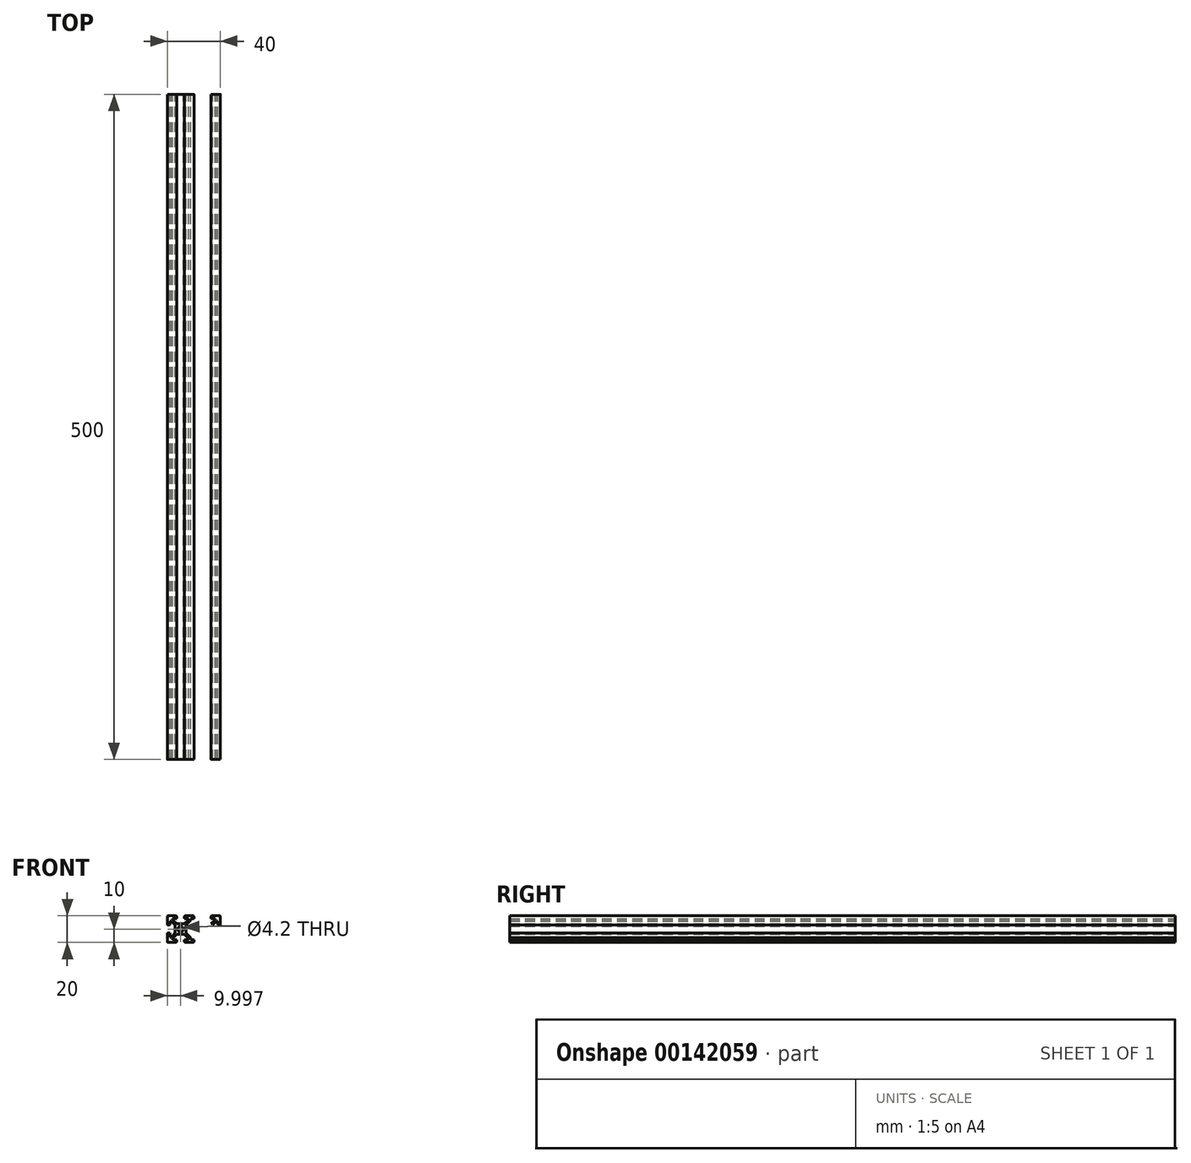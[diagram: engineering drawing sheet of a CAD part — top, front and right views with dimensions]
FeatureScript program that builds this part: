
annotation { "Feature Type Name" : "Feature", "Feature Type Description" : "" }
export const myFeature = defineFeature(function(context is Context, id is Id, definition is map)
    precondition{}
    {
        {
            var Q0;
            Q0=qCreatedBy(makeId("Front.planeOp"),FACE);
            var sketch = newSketch(context, id + "F0", { "sketchPlane" : qUnion([Q0])});
            skLineSegment(sketch, "E0.bottom", {"start": v(-257.68, 19.3) * mm, "end": v(-217.68, 19.3) * mm});
            skLineSegment(sketch, "E0.top", {"start": v(-257.68, -0.7) * mm, "end": v(-217.68, -0.7) * mm});
            skLineSegment(sketch, "E0.left", {"start": v(-257.68, 19.3) * mm, "end": v(-257.68, -0.7) * mm});
            skLineSegment(sketch, "E0.right", {"start": v(-217.68, 19.3) * mm, "end": v(-217.68, -0.7) * mm});
            skLineSegment(sketch, "E1.bottom", {"start": v(-251.68, 13.3) * mm, "end": v(-243.68, 13.3) * mm});
            skLineSegment(sketch, "E1.top", {"start": v(-251.68, 5.3) * mm, "end": v(-243.68, 5.3) * mm});
            skLineSegment(sketch, "E1.left", {"start": v(-251.68, 13.3) * mm, "end": v(-251.68, 5.3) * mm});
            skLineSegment(sketch, "E1.right", {"start": v(-243.68, 13.3) * mm, "end": v(-243.68, 5.3) * mm});
            skLineSegment(sketch, "E2.bottom", {"start": v(-231.68, 13.3) * mm, "end": v(-223.68, 13.3) * mm});
            skLineSegment(sketch, "E2.top", {"start": v(-231.68, 5.3) * mm, "end": v(-223.68, 5.3) * mm});
            skLineSegment(sketch, "E2.left", {"start": v(-231.68, 13.3) * mm, "end": v(-231.68, 5.3) * mm});
            skLineSegment(sketch, "E2.right", {"start": v(-223.68, 13.3) * mm, "end": v(-223.68, 5.3) * mm});
            skCircle(sketch, "E3", {"center": v(-247.68, 9.3) * mm, "radius": 4 * mm});
            skPoint(sketch, "E3.first.point", {"position": v(-251.68, 9.3) * mm});
            skPoint(sketch, "E3.second.point", {"position": v(-247.68, 5.3) * mm});
            skPoint(sketch, "E3.third.point", {"position": v(-243.68, 9.3) * mm});
            skCircle(sketch, "E4", {"center": v(-227.68, 9.3) * mm, "radius": 4 * mm});
            skPoint(sketch, "E4.first.point", {"position": v(-227.68, 5.3) * mm});
            skPoint(sketch, "E4.second.point", {"position": v(-231.68, 9.3) * mm});
            skPoint(sketch, "E4.third.point", {"position": v(-227.68, 13.3) * mm});
            skCircle(sketch, "E5", {"center": v(-247.68, 9.3) * mm, "radius": 2.1 * mm});
            skCircle(sketch, "E6", {"center": v(-227.68, 9.3) * mm, "radius": 2.1 * mm});
            skLineSegment(sketch, "E7.bottom", {"start": v(-250.68, -0.7) * mm, "end": v(-244.68, -0.7) * mm});
            skLineSegment(sketch, "E7.top", {"start": v(-250.68, 1.3) * mm, "end": v(-244.68, 1.3) * mm});
            skLineSegment(sketch, "E7.left", {"start": v(-250.68, -0.7) * mm, "end": v(-250.68, 1.3) * mm});
            skLineSegment(sketch, "E7.right", {"start": v(-244.68, -0.7) * mm, "end": v(-244.68, 1.3) * mm});
            skLineSegment(sketch, "E8.bottom", {"start": v(-230.68, -0.7) * mm, "end": v(-224.68, -0.7) * mm});
            skLineSegment(sketch, "E8.top", {"start": v(-230.68, 1.3) * mm, "end": v(-224.68, 1.3) * mm});
            skLineSegment(sketch, "E8.left", {"start": v(-230.68, -0.7) * mm, "end": v(-230.68, 1.3) * mm});
            skLineSegment(sketch, "E8.right", {"start": v(-224.68, -0.7) * mm, "end": v(-224.68, 1.3) * mm});
            skLineSegment(sketch, "E9.bottom", {"start": v(-217.68, 6.3) * mm, "end": v(-219.68, 6.3) * mm});
            skLineSegment(sketch, "E9.top", {"start": v(-217.68, 12.3) * mm, "end": v(-219.68, 12.3) * mm});
            skLineSegment(sketch, "E9.left", {"start": v(-217.68, 6.3) * mm, "end": v(-217.68, 12.3) * mm});
            skLineSegment(sketch, "E9.right", {"start": v(-219.68, 6.3) * mm, "end": v(-219.68, 12.3) * mm});
            skLineSegment(sketch, "E10.bottom", {"start": v(-224.68, 19.3) * mm, "end": v(-230.68, 19.3) * mm});
            skLineSegment(sketch, "E10.top", {"start": v(-224.68, 17.3) * mm, "end": v(-230.68, 17.3) * mm});
            skLineSegment(sketch, "E10.left", {"start": v(-224.68, 19.3) * mm, "end": v(-224.68, 17.3) * mm});
            skLineSegment(sketch, "E10.right", {"start": v(-230.68, 19.3) * mm, "end": v(-230.68, 17.3) * mm});
            skLineSegment(sketch, "E11.bottom", {"start": v(-244.68, 19.3) * mm, "end": v(-250.68, 19.3) * mm});
            skLineSegment(sketch, "E11.top", {"start": v(-244.68, 17.3) * mm, "end": v(-250.68, 17.3) * mm});
            skLineSegment(sketch, "E11.left", {"start": v(-244.68, 19.3) * mm, "end": v(-244.68, 17.3) * mm});
            skLineSegment(sketch, "E11.right", {"start": v(-250.68, 19.3) * mm, "end": v(-250.68, 17.3) * mm});
            skLineSegment(sketch, "E12.bottom", {"start": v(-257.68, 6.3) * mm, "end": v(-255.68, 6.3) * mm});
            skLineSegment(sketch, "E12.top", {"start": v(-257.68, 12.3) * mm, "end": v(-255.68, 12.3) * mm});
            skLineSegment(sketch, "E12.left", {"start": v(-257.68, 6.3) * mm, "end": v(-257.68, 12.3) * mm});
            skLineSegment(sketch, "E12.right", {"start": v(-255.68, 6.3) * mm, "end": v(-255.68, 12.3) * mm});
            skLineSegment(sketch, "E13", {"start": v(-250.68, 17.3) * mm, "end": v(-253.68, 17.3) * mm});
            skLineSegment(sketch, "E14", {"start": v(-253.68, 17.3) * mm, "end": v(-253.68, 16.3) * mm});
            skLineSegment(sketch, "E15", {"start": v(-253.68, 16.3) * mm, "end": v(-250.68, 13.3) * mm});
            skLineSegment(sketch, "E16", {"start": v(-244.68, 17.3) * mm, "end": v(-241.68, 17.3) * mm});
            skLineSegment(sketch, "E17", {"start": v(-241.68, 17.3) * mm, "end": v(-241.68, 16.3) * mm});
            skLineSegment(sketch, "E18", {"start": v(-241.68, 16.3) * mm, "end": v(-244.68, 13.3) * mm});
            skLineSegment(sketch, "E19", {"start": v(-257.68, 9.3) * mm, "end": v(-217.68, 9.3) * mm});
            skLineSegment(sketch, "E20", {"start": v(-237.68, 19.3) * mm, "end": v(-237.68, -0.7) * mm});
            skLineSegment(sketch, "E21.MirrorCS", {"start": v(-253.68, 2.3) * mm, "end": v(-250.68, 5.3) * mm});
            skLineSegment(sketch, "E22.MirrorCS", {"start": v(-253.68, 1.3) * mm, "end": v(-253.68, 2.3) * mm});
            skLineSegment(sketch, "E23.MirrorCS", {"start": v(-244.68, 1.3) * mm, "end": v(-250.68, 1.3) * mm});
            skLineSegment(sketch, "E24.MirrorCS", {"start": v(-250.68, 1.3) * mm, "end": v(-253.68, 1.3) * mm});
            skLineSegment(sketch, "E25.MirrorCS", {"start": v(-241.68, 1.3) * mm, "end": v(-241.68, 2.3) * mm});
            skLineSegment(sketch, "E26.MirrorCS", {"start": v(-241.68, 2.3) * mm, "end": v(-244.68, 5.3) * mm});
            skLineSegment(sketch, "E27.MirrorCS", {"start": v(-244.68, 1.3) * mm, "end": v(-241.68, 1.3) * mm});
            skLineSegment(sketch, "E28", {"start": v(-255.68, 12.3) * mm, "end": v(-255.68, 15.3) * mm});
            skLineSegment(sketch, "E29", {"start": v(-255.68, 15.3) * mm, "end": v(-254.68, 15.3) * mm});
            skLineSegment(sketch, "E30", {"start": v(-254.68, 15.3) * mm, "end": v(-251.68, 12.3) * mm});
            skLineSegment(sketch, "E31", {"start": v(-255.68, 6.3) * mm, "end": v(-255.68, 3.3) * mm});
            skLineSegment(sketch, "E32", {"start": v(-255.68, 3.3) * mm, "end": v(-254.68, 3.3) * mm});
            skLineSegment(sketch, "E33", {"start": v(-254.68, 3.3) * mm, "end": v(-251.68, 6.3) * mm});
            skLineSegment(sketch, "E34.MirrorCS", {"start": v(-219.68, 15.3) * mm, "end": v(-220.68, 15.3) * mm});
            skLineSegment(sketch, "E35.MirrorCS", {"start": v(-221.68, 17.3) * mm, "end": v(-221.68, 16.3) * mm});
            skLineSegment(sketch, "E36.MirrorCS", {"start": v(-221.68, 1.3) * mm, "end": v(-221.68, 2.3) * mm});
            skLineSegment(sketch, "E37.MirrorCS", {"start": v(-233.68, 1.3) * mm, "end": v(-233.68, 2.3) * mm});
            skLineSegment(sketch, "E38.MirrorCS", {"start": v(-219.68, 3.3) * mm, "end": v(-220.68, 3.3) * mm});
            skLineSegment(sketch, "E39.MirrorCS", {"start": v(-233.68, 17.3) * mm, "end": v(-233.68, 16.3) * mm});
            skLineSegment(sketch, "E40.MirrorCS", {"start": v(-223.68, 5.3) * mm, "end": v(-231.68, 5.3) * mm});
            skLineSegment(sketch, "E41.MirrorCS", {"start": v(-219.68, 6.3) * mm, "end": v(-219.68, 3.3) * mm});
            skLineSegment(sketch, "E42.MirrorCS", {"start": v(-224.68, 1.3) * mm, "end": v(-230.68, 1.3) * mm});
            skLineSegment(sketch, "E43.MirrorCS", {"start": v(-219.68, 12.3) * mm, "end": v(-219.68, 15.3) * mm});
            skLineSegment(sketch, "E44.MirrorCS", {"start": v(-220.68, 15.3) * mm, "end": v(-223.68, 12.3) * mm});
            skLineSegment(sketch, "E45.MirrorCS", {"start": v(-221.68, 16.3) * mm, "end": v(-224.68, 13.3) * mm});
            skLineSegment(sketch, "E46.MirrorCS", {"start": v(-230.68, 17.3) * mm, "end": v(-233.68, 17.3) * mm});
            skLineSegment(sketch, "E47.MirrorCS", {"start": v(-230.68, 17.3) * mm, "end": v(-224.68, 17.3) * mm});
            skLineSegment(sketch, "E48.MirrorCS", {"start": v(-223.68, 13.3) * mm, "end": v(-231.68, 13.3) * mm});
            skLineSegment(sketch, "E49.MirrorCS", {"start": v(-224.68, 17.3) * mm, "end": v(-221.68, 17.3) * mm});
            skLineSegment(sketch, "E50.MirrorCS", {"start": v(-233.68, 2.3) * mm, "end": v(-230.68, 5.3) * mm});
            skLineSegment(sketch, "E51.MirrorCS", {"start": v(-230.68, 19.3) * mm, "end": v(-224.68, 19.3) * mm});
            skLineSegment(sketch, "E52.MirrorCS", {"start": v(-221.68, 2.3) * mm, "end": v(-224.68, 5.3) * mm});
            skLineSegment(sketch, "E53.MirrorCS", {"start": v(-224.68, -0.7) * mm, "end": v(-230.68, -0.7) * mm});
            skLineSegment(sketch, "E54.MirrorCS", {"start": v(-230.68, 1.3) * mm, "end": v(-233.68, 1.3) * mm});
            skPoint(sketch, "E55.MirrorP", {"position": v(-223.68, 9.3) * mm});
            skLineSegment(sketch, "E56.MirrorCS", {"start": v(-233.68, 16.3) * mm, "end": v(-230.68, 13.3) * mm});
            skLineSegment(sketch, "E57.MirrorCS", {"start": v(-224.68, 1.3) * mm, "end": v(-221.68, 1.3) * mm});
            skLineSegment(sketch, "E58.MirrorCS", {"start": v(-220.68, 3.3) * mm, "end": v(-223.68, 6.3) * mm});
            skLineSegment(sketch, "E59", {"start": v(-240.18, 1.3) * mm, "end": v(-235.18, 1.3) * mm});
            skLineSegment(sketch, "E60", {"start": v(-235.18, 1.3) * mm, "end": v(-235.18, 2.8) * mm});
            skLineSegment(sketch, "E61", {"start": v(-235.18, 2.8) * mm, "end": v(-231.68, 6.3) * mm});
            skLineSegment(sketch, "E62", {"start": v(-240.18, 1.3) * mm, "end": v(-240.18, 2.8) * mm});
            skLineSegment(sketch, "E63", {"start": v(-240.18, 2.8) * mm, "end": v(-243.68, 6.3) * mm});
            skLineSegment(sketch, "E64.MirrorCS", {"start": v(-240.18, 17.3) * mm, "end": v(-235.18, 17.3) * mm});
            skLineSegment(sketch, "E65.MirrorCS", {"start": v(-235.18, 17.3) * mm, "end": v(-235.18, 15.8) * mm});
            skLineSegment(sketch, "E66.MirrorCS", {"start": v(-235.18, 15.8) * mm, "end": v(-231.68, 12.3) * mm});
            skLineSegment(sketch, "E67.MirrorCS", {"start": v(-240.18, 17.3) * mm, "end": v(-240.18, 15.8) * mm});
            skLineSegment(sketch, "E68.MirrorCS", {"start": v(-240.18, 15.8) * mm, "end": v(-243.68, 12.3) * mm});
            skSolve(sketch);
        }
        {
            var Q0;
            {var subQ2=sQuery(id+"F0.wireOp",EDGE,"E11.right");Q0=makeQuery(id+"F0.imprint","IMPRINT",FACE,{"disambiguationData":[TD([[makeQuery(id+"F0.imprint","IMPRINT",EDGE,{"derivedFrom":subQ2}),-1.0]])]});}
            var Q1;
            {var subQ9=sQuery(id+"F0.wireOp",EDGE,"E7.left");Q1=makeQuery(id+"F0.imprint","IMPRINT",FACE,{"disambiguationData":[TD([[makeQuery(id+"F0.imprint","IMPRINT",EDGE,{"derivedFrom":subQ9}),1.0]])]});}
            var Q2;
            {var subQ11=sQuery(id+"F0.wireOp",EDGE,"E7.right");Q2=makeQuery(id+"F0.imprint","IMPRINT",FACE,{"disambiguationData":[TD([[makeQuery(id+"F0.imprint","IMPRINT",EDGE,{"derivedFrom":subQ11}),-1.0]])]});}
            var Q3;
            {var subQ11=sQuery(id+"F0.wireOp",EDGE,"E8.left");Q3=makeQuery(id+"F0.imprint","IMPRINT",FACE,{"disambiguationData":[TD([[makeQuery(id+"F0.imprint","IMPRINT",EDGE,{"derivedFrom":subQ11}),1.0]])]});}
            var Q4;
            {var subQ9=sQuery(id+"F0.wireOp",EDGE,"E8.right");Q4=makeQuery(id+"F0.imprint","IMPRINT",FACE,{"disambiguationData":[TD([[makeQuery(id+"F0.imprint","IMPRINT",EDGE,{"derivedFrom":subQ9}),-1.0]])]});}
            var Q5;
            Q5=makeQuery(id+"F0.imprint","IMPRINT",FACE,{"disambiguationData":[TD([[makeQuery(id+"F0.imprint","IMPRINT",EDGE,{"derivedFrom":sQuery(id+"F0.wireOp",EDGE,"E34.MirrorCS")}),-1.0]])]});
            var Q6;
            {var subQ9=sQuery(id+"F0.wireOp",EDGE,"E10.right");Q6=makeQuery(id+"F0.imprint","IMPRINT",FACE,{"disambiguationData":[TD([[makeQuery(id+"F0.imprint","IMPRINT",EDGE,{"derivedFrom":subQ9}),-1.0]])]});}
            var Q7;
            {var subQ9=sQuery(id+"F0.wireOp",EDGE,"E11.left");Q7=makeQuery(id+"F0.imprint","IMPRINT",FACE,{"disambiguationData":[TD([[makeQuery(id+"F0.imprint","IMPRINT",EDGE,{"derivedFrom":subQ9}),1.0]])]});}
            var Q8;
            {var subQ4=sQuery(id+"F0.wireOp",EDGE,"E1.bottom");var subQ6=makeQuery(id+"F0.imprint","INTERSECT",VERTEX,{"derivedFrom":[subQ4,sQuery(id+"F0.wireOp",EDGE,"E18")]});Q8=makeQuery(id+"F0.imprint","IMPRINT",FACE,{"disambiguationData":[TD([[makeQuery(id+"F0.imprint","IMPRINT",EDGE,{"disambiguationData":[TD([[subQ6,1.0]])],"derivedFrom":subQ4}),-1.0]])]});}
            var Q9;
            {var subQ0=sQuery(id+"F0.wireOp",EDGE,"E1.left");var subQ4=sQuery(id+"F0.wireOp",EDGE,"E1.bottom");var subQ5=makeQuery(id+"F0.imprint","INTERSECT",VERTEX,{"derivedFrom":[subQ4,subQ0]});Q9=makeQuery(id+"F0.imprint","IMPRINT",FACE,{"disambiguationData":[TD([[makeQuery(id+"F0.imprint","IMPRINT",EDGE,{"disambiguationData":[TD([[subQ5,-1.0]])],"derivedFrom":subQ4}),-1.0]])]});}
            var Q10;
            {var subQ0=sQuery(id+"F0.wireOp",EDGE,"E19");var subQ1=sQuery(id+"F0.wireOp",EDGE,"E5");var subQ2=makeQuery(id+"F0.imprint","INTERSECT",VERTEX,{"disambiguationData":[OD(0.0)],"derivedFrom":[subQ1,subQ0]});Q10=makeQuery(id+"F0.imprint","IMPRINT",FACE,{"disambiguationData":[TD([[makeQuery(id+"F0.imprint","IMPRINT",EDGE,{"disambiguationData":[TD([[subQ2,1.0]])],"derivedFrom":subQ1}),-1.0]])]});}
            var Q11;
            {var subQ0=sQuery(id+"F0.wireOp",EDGE,"E1.top");var subQ1=sQuery(id+"F0.wireOp",EDGE,"E1.left");var subQ2=makeQuery(id+"F0.imprint","INTERSECT",VERTEX,{"derivedFrom":[subQ1,subQ0]});Q11=makeQuery(id+"F0.imprint","IMPRINT",FACE,{"disambiguationData":[TD([[makeQuery(id+"F0.imprint","IMPRINT",EDGE,{"disambiguationData":[TD([[subQ2,1.0]])],"derivedFrom":subQ1}),1.0]])]});}
            var Q12;
            {var subQ0=sQuery(id+"F0.wireOp",EDGE,"E1.top");var subQ3=sQuery(id+"F0.wireOp",EDGE,"E1.right");var subQ6=makeQuery(id+"F0.imprint","INTERSECT",VERTEX,{"derivedFrom":[subQ3,subQ0]});Q12=makeQuery(id+"F0.imprint","IMPRINT",FACE,{"disambiguationData":[TD([[makeQuery(id+"F0.imprint","IMPRINT",EDGE,{"disambiguationData":[TD([[subQ6,1.0]])],"derivedFrom":subQ3}),-1.0]])]});}
            var Q13;
            {var subQ2=sQuery(id+"F0.wireOp",EDGE,"E19");var subQ4=sQuery(id+"F0.wireOp",EDGE,"E6");var subQ6=makeQuery(id+"F0.imprint","INTERSECT",VERTEX,{"disambiguationData":[OD(0.0)],"derivedFrom":[subQ2,subQ4]});Q13=makeQuery(id+"F0.imprint","IMPRINT",FACE,{"disambiguationData":[TD([[makeQuery(id+"F0.imprint","IMPRINT",EDGE,{"disambiguationData":[TD([[subQ6,1.0]])],"derivedFrom":subQ4}),1.0]])]});}
            var Q14;
            {var subQ4=sQuery(id+"F0.wireOp",EDGE,"E40.MirrorCS");var subQ7=makeQuery(id+"F0.imprint","INTERSECT",VERTEX,{"derivedFrom":[subQ4,sQuery(id+"F0.wireOp",EDGE,"E50.MirrorCS")]});Q14=makeQuery(id+"F0.imprint","IMPRINT",FACE,{"disambiguationData":[TD([[makeQuery(id+"F0.imprint","IMPRINT",EDGE,{"disambiguationData":[TD([[subQ7,1.0]])],"derivedFrom":subQ4}),-1.0]])]});}
            var Q15;
            {var subQ0=sQuery(id+"F0.wireOp",EDGE,"E40.MirrorCS");var subQ4=sQuery(id+"F0.wireOp",EDGE,"E2.right");var subQ5=makeQuery(id+"F0.imprint","INTERSECT",VERTEX,{"derivedFrom":[subQ4,subQ0]});Q15=makeQuery(id+"F0.imprint","IMPRINT",FACE,{"disambiguationData":[TD([[makeQuery(id+"F0.imprint","IMPRINT",EDGE,{"disambiguationData":[TD([[subQ5,1.0]])],"derivedFrom":subQ4}),-1.0]])]});}
            var Q16;
            {var subQ4=sQuery(id+"F0.wireOp",EDGE,"E2.right");var subQ6=makeQuery(id+"F0.imprint","INTERSECT",VERTEX,{"derivedFrom":[sQuery(id+"F0.wireOp",EDGE,"E44.MirrorCS"),subQ4]});Q16=makeQuery(id+"F0.imprint","IMPRINT",FACE,{"disambiguationData":[TD([[makeQuery(id+"F0.imprint","IMPRINT",EDGE,{"disambiguationData":[TD([[subQ6,1.0]])],"derivedFrom":subQ4}),-1.0]])]});}
            var Q17;
            {var subQ2=sQuery(id+"F0.wireOp",EDGE,"E19");var subQ4=sQuery(id+"F0.wireOp",EDGE,"E6");var subQ5=makeQuery(id+"F0.imprint","INTERSECT",VERTEX,{"disambiguationData":[OD(0.0)],"derivedFrom":[subQ2,subQ4]});Q17=makeQuery(id+"F0.imprint","IMPRINT",FACE,{"disambiguationData":[TD([[makeQuery(id+"F0.imprint","IMPRINT",EDGE,{"disambiguationData":[TD([[subQ5,-1.0]])],"derivedFrom":subQ4}),1.0]])]});}
            var Q18;
            {var subQ1=sQuery(id+"F0.wireOp",EDGE,"E48.MirrorCS");var subQ7=makeQuery(id+"F0.imprint","INTERSECT",VERTEX,{"derivedFrom":[subQ1,sQuery(id+"F0.wireOp",EDGE,"E56.MirrorCS")]});Q18=makeQuery(id+"F0.imprint","IMPRINT",FACE,{"disambiguationData":[TD([[makeQuery(id+"F0.imprint","IMPRINT",EDGE,{"disambiguationData":[TD([[subQ7,1.0]])],"derivedFrom":subQ1}),1.0]])]});}
            var Q19;
            {var subQ0=sQuery(id+"F0.wireOp",EDGE,"E19");var subQ1=sQuery(id+"F0.wireOp",EDGE,"E5");var subQ2=makeQuery(id+"F0.imprint","INTERSECT",VERTEX,{"disambiguationData":[OD(0.0)],"derivedFrom":[subQ1,subQ0]});Q19=makeQuery(id+"F0.imprint","IMPRINT",FACE,{"disambiguationData":[TD([[makeQuery(id+"F0.imprint","IMPRINT",EDGE,{"disambiguationData":[TD([[subQ2,-1.0]])],"derivedFrom":subQ1}),-1.0]])]});}
            extrude(context, id + "F1", {"entities" : qUnion([Q0, Q1, Q2, Q3, Q4, Q5, Q6, Q7, Q8, Q9, Q10, Q11, Q12, Q13, Q14, Q15, Q16, Q17, Q18, Q19]), "depth" : 500 * mm});
        }
        {
            var Q0;
            Q0=makeQuery(id+"F1.opExtrude","SWEPT_EDGE",EDGE,{"disambiguationData":[OSD([sQuery(id+"F0.wireOp",EDGE,"E0.bottom"),sQuery(id+"F0.wireOp",EDGE,"E0.left")])]});
            var Q1;
            Q1=makeQuery(id+"F1.opExtrude","SWEPT_EDGE",EDGE,{"disambiguationData":[OSD([sQuery(id+"F0.wireOp",EDGE,"E0.bottom"),sQuery(id+"F0.wireOp",EDGE,"E11.bottom"),sQuery(id+"F0.wireOp",EDGE,"E11.right")])]});
            var Q2;
            Q2=makeQuery(id+"F1.opExtrude","SWEPT_EDGE",EDGE,{"disambiguationData":[OSD([sQuery(id+"F0.wireOp",EDGE,"E0.bottom"),sQuery(id+"F0.wireOp",EDGE,"E11.bottom"),sQuery(id+"F0.wireOp",EDGE,"E11.left")])]});
            var Q3;
            Q3=makeQuery(id+"F1.opExtrude","SWEPT_EDGE",EDGE,{"disambiguationData":[OSD([sQuery(id+"F0.wireOp",EDGE,"E0.bottom"),sQuery(id+"F0.wireOp",EDGE,"E10.right"),sQuery(id+"F0.wireOp",EDGE,"E51.MirrorCS")])]});
            var Q4;
            Q4=makeQuery(id+"F1.opExtrude","SWEPT_EDGE",EDGE,{"disambiguationData":[OSD([sQuery(id+"F0.wireOp",EDGE,"E0.bottom"),sQuery(id+"F0.wireOp",EDGE,"E10.left"),sQuery(id+"F0.wireOp",EDGE,"E51.MirrorCS")])]});
            var Q5;
            Q5=makeQuery(id+"F1.opExtrude","SWEPT_EDGE",EDGE,{"disambiguationData":[OSD([sQuery(id+"F0.wireOp",EDGE,"E0.bottom"),sQuery(id+"F0.wireOp",EDGE,"E0.right")])]});
            var Q6;
            Q6=makeQuery(id+"F1.opExtrude","SWEPT_EDGE",EDGE,{"disambiguationData":[OSD([sQuery(id+"F0.wireOp",EDGE,"E9.top"),sQuery(id+"F0.wireOp",EDGE,"E0.right")])]});
            var Q7;
            Q7=makeQuery(id+"F1.opExtrude","SWEPT_EDGE",EDGE,{"disambiguationData":[OSD([sQuery(id+"F0.wireOp",EDGE,"E9.bottom"),sQuery(id+"F0.wireOp",EDGE,"E0.right")])]});
            var Q8;
            Q8=makeQuery(id+"F1.opExtrude","SWEPT_EDGE",EDGE,{"disambiguationData":[OSD([sQuery(id+"F0.wireOp",EDGE,"E0.top"),sQuery(id+"F0.wireOp",EDGE,"E0.right")])]});
            var Q9;
            Q9=makeQuery(id+"F1.opExtrude","SWEPT_EDGE",EDGE,{"disambiguationData":[OSD([sQuery(id+"F0.wireOp",EDGE,"E0.top"),sQuery(id+"F0.wireOp",EDGE,"E8.left"),sQuery(id+"F0.wireOp",EDGE,"E53.MirrorCS")])]});
            var Q10;
            Q10=makeQuery(id+"F1.opExtrude","SWEPT_EDGE",EDGE,{"disambiguationData":[OSD([sQuery(id+"F0.wireOp",EDGE,"E0.top"),sQuery(id+"F0.wireOp",EDGE,"E7.bottom"),sQuery(id+"F0.wireOp",EDGE,"E7.left")])]});
            var Q11;
            Q11=makeQuery(id+"F1.opExtrude","SWEPT_EDGE",EDGE,{"disambiguationData":[OSD([sQuery(id+"F0.wireOp",EDGE,"E0.left"),sQuery(id+"F0.wireOp",EDGE,"E12.bottom"),sQuery(id+"F0.wireOp",EDGE,"E12.left")])]});
            var Q12;
            Q12=makeQuery(id+"F1.opExtrude","SWEPT_EDGE",EDGE,{"disambiguationData":[OSD([sQuery(id+"F0.wireOp",EDGE,"E0.left"),sQuery(id+"F0.wireOp",EDGE,"E12.top"),sQuery(id+"F0.wireOp",EDGE,"E12.left")])]});
            var Q13;
            Q13=makeQuery(id+"F1.opExtrude","SWEPT_EDGE",EDGE,{"disambiguationData":[OSD([sQuery(id+"F0.wireOp",EDGE,"E0.top"),sQuery(id+"F0.wireOp",EDGE,"E0.left")])]});
            var Q14;
            Q14=makeQuery(id+"F1.opExtrude","SWEPT_EDGE",EDGE,{"disambiguationData":[OSD([sQuery(id+"F0.wireOp",EDGE,"E0.top"),sQuery(id+"F0.wireOp",EDGE,"E7.bottom"),sQuery(id+"F0.wireOp",EDGE,"E7.right")])]});
            var Q15;
            Q15=makeQuery(id+"F1.opExtrude","SWEPT_EDGE",EDGE,{"disambiguationData":[OSD([sQuery(id+"F0.wireOp",EDGE,"E0.top"),sQuery(id+"F0.wireOp",EDGE,"E8.right"),sQuery(id+"F0.wireOp",EDGE,"E53.MirrorCS")])]});
            fillet(context, id + "F2", {"entities" : qUnion([Q0, Q1, Q2, Q3, Q4, Q5, Q6, Q7, Q8, Q9, Q10, Q11, Q12, Q13, Q14, Q15]), "radius" : 0.5 * mm, "tangentPropagation" : true, "allowEdgeOverflow" : false});
        }
    });
